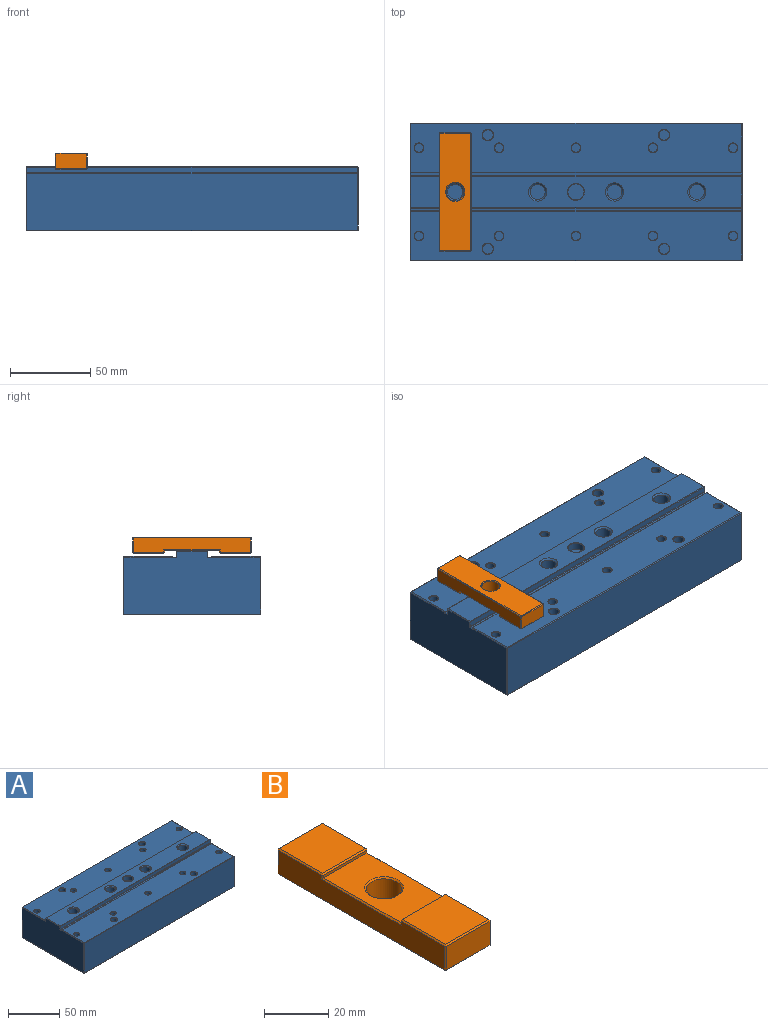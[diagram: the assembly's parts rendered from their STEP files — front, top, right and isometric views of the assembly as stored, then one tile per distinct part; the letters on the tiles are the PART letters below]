
ASSEMBLY  parts=2 mates=1
PART A: 127 faces, bbox 207.1x86x40 mm
  f0: plane 206.1x85mm, normal (0,0,-1), area 17314.4mm2, adj f68,f69,f79,f80,f110,f111
  f1: plane 206.1x30.37mm, normal (0,0,1), area 6032.9mm2, adj f10,f77,f86,f93,f120,f121,f122,f123
  f2: plane 85x39mm, normal (1,0,0), area 3080.9mm2, adj f58,f59,f60,f61,f62,f63,f65,f67
  f3: plane 85x39mm, normal (-1,0,0), area 3080.9mm2, adj f80,f81,f87,f88,f91,f93,f94,f95
  f4: plane 206.1x30.37mm, normal (0,0,1), area 6032.9mm2, adj f8,f71,f82,f88,f113,f114,f115,f116
  f5: plane 206.1x19.27mm, normal (0,0,1), area 3475mm2, adj f20,f21,f22,f23,f59,f100,f102,f103
  f6: plane 206.1x3.4mm, normal (0,-1,0), area 700.7mm2, adj f25,f61,f101,f103
  f7: plane 206.1x3.4mm, normal (0,1,0), area 700.7mm2, adj f27,f58,f98,f102
  f8: plane 206.1x0.2mm, normal (0,-1,0), area 41.2mm2, adj f4,f26,f66,f89
  f9: plane 206.1x1.6mm, normal (0,0,1), area 329.8mm2, adj f26,f27,f62,f94
  f10: plane 206.1x0.2mm, normal (0,1,0), area 41.2mm2, adj f1,f24,f72,f92
  f11: plane 206.1x1.6mm, normal (0,0,1), area 329.8mm2, adj f24,f25,f67,f97
  f12: cylinder r=4.7mm len=24mm, axis (0,0,1), area 708.7mm2, adj f13,f20
  f13: plane 9.4x9.4mm, normal (0,0,1), area 69.4mm2, adj f12
  f14: cylinder r=4.7mm len=24mm, axis (0,0,1), area 708.7mm2, adj f15,f21
  f15: plane 9.4x9.4mm, normal (0,0,1), area 69.4mm2, adj f14
  f16: cylinder r=4.7mm len=24mm, axis (0,0,1), area 708.7mm2, adj f17,f22
  f17: plane 9.4x9.4mm, normal (0,0,1), area 69.4mm2, adj f16
  f18: cylinder r=4.7mm len=24mm, axis (0,0,1), area 708.7mm2, adj f19,f23
  f19: plane 9.4x9.4mm, normal (0,0,1), area 69.4mm2, adj f18
  f20: cone r=5.7mm half-angle=45deg, axis (0,0,1), area 46.2mm2, adj f5,f12
  f21: cone r=5.7mm half-angle=45deg, axis (0,0,1), area 46.2mm2, adj f5,f14
  f22: cone r=4.7mm half-angle=45deg, axis (0,0,1), area 46.2mm2, adj f5,f16
  f23: cone r=4.7mm half-angle=45deg, axis (0,0,1), area 46.2mm2, adj f5,f18
  f24: cylinder r=0.3mm len=206.1mm, axis (1,0,0), area 97.1mm2, adj f10,f11,f73,f95
  f25: cylinder r=0.3mm len=206.1mm, axis (-1,0,0), area 97.1mm2, adj f6,f11,f63,f99
  f26: cylinder r=0.3mm len=206.1mm, axis (-1,0,0), area 97.1mm2, adj f8,f9,f65,f91
  f27: cylinder r=0.3mm len=206.1mm, axis (1,0,0), area 97.1mm2, adj f7,f9,f60,f96
  f28: cylinder r=3.25mm len=6.5mm, axis (0,0,1), area 96mm2, adj f29,f114
  f29: plane 6.5x6.5mm, normal (0,0,1), area 33.2mm2, adj f28
  f30: cylinder r=2.75mm len=5.5mm, axis (0,0,1), area 81.2mm2, adj f31,f116
  f31: plane 5.5x5.5mm, normal (0,0,1), area 23.8mm2, adj f30
  f32: cylinder r=2.75mm len=5.5mm, axis (0,0,1), area 81.2mm2, adj f33,f119
  f33: plane 5.5x5.5mm, normal (0,0,1), area 23.8mm2, adj f32
  f34: cylinder r=3.25mm len=6.5mm, axis (0,0,1), area 96mm2, adj f35,f118
  f35: plane 6.5x6.5mm, normal (0,0,1), area 33.2mm2, adj f34
  f36: cylinder r=2.75mm len=5.5mm, axis (0,0,1), area 81.2mm2, adj f37,f117
  f37: plane 5.5x5.5mm, normal (0,0,1), area 23.8mm2, adj f36
  f38: cylinder r=2.75mm len=5.5mm, axis (0,0,1), area 81.2mm2, adj f39,f113
  f39: plane 5.5x5.5mm, normal (0,0,1), area 23.8mm2, adj f38
  f40: cylinder r=2.75mm len=5.5mm, axis (0,0,1), area 81.2mm2, adj f41,f115
  f41: plane 5.5x5.5mm, normal (0,0,1), area 23.8mm2, adj f40
  f42: cylinder r=2.75mm len=5.5mm, axis (0,0,1), area 81.2mm2, adj f43,f123
  f43: plane 5.5x5.5mm, normal (0,0,1), area 23.8mm2, adj f42
  f44: cylinder r=2.75mm len=5.5mm, axis (0,0,1), area 81.2mm2, adj f45,f120
  f45: plane 5.5x5.5mm, normal (0,0,1), area 23.8mm2, adj f44
  f46: cylinder r=2.75mm len=5.5mm, axis (0,0,1), area 81.2mm2, adj f47,f124
  f47: plane 5.5x5.5mm, normal (0,0,1), area 23.8mm2, adj f46
  f48: cylinder r=3.25mm len=6.5mm, axis (0,0,1), area 96mm2, adj f49,f125
  f49: plane 6.5x6.5mm, normal (0,0,1), area 33.2mm2, adj f48
  f50: cylinder r=2.75mm len=5.5mm, axis (0,0,1), area 81.2mm2, adj f51,f122
  f51: plane 5.5x5.5mm, normal (0,0,1), area 23.8mm2, adj f50
  f52: cylinder r=3.25mm len=6.5mm, axis (0,0,1), area 96mm2, adj f53,f121
  f53: plane 6.5x6.5mm, normal (0,0,1), area 33.2mm2, adj f52
  f54: cylinder r=2.75mm len=5.5mm, axis (0,0,1), area 81.2mm2, adj f55,f126
  f55: plane 5.5x5.5mm, normal (0,0,1), area 23.8mm2, adj f54
  f56: plane 206.1x35.5mm, normal (0,-1,0), area 7316.6mm2, adj f78,f79,f86,f87
  f57: plane 206.1x35.5mm, normal (0,1,0), area 7316.6mm2, adj f69,f70,f81,f82
  f58: plane 3.55x0.5mm, normal (0.71,0.71,0), area 2.4mm2, adj f2,f7,f59,f60,f102
  f59: plane 19.57x0.5mm, normal (0.71,0,0.71), area 13.6mm2, adj f2,f5,f58,f61,f102,f103
  f60: cone r=0.8mm half-angle=45deg, axis (1,0,0), area 0.6mm2, adj f2,f27,f58,f62
  f61: plane 3.55x0.5mm, normal (0.71,-0.71,0), area 2.4mm2, adj f2,f6,f59,f63,f103
  f62: plane 1.6x0.5mm, normal (0.71,0,0.71), area 1.1mm2, adj f2,f9,f60,f65
  f63: cone r=0.8mm half-angle=45deg, axis (1,0,0), area 0.6mm2, adj f2,f25,f61,f67
  f64: plane 0.5x0.5mm, normal (0.58,0.58,-0.58), area 0.2mm2, adj f68,f69,f70
  f65: cone r=0.8mm half-angle=45deg, axis (1,0,0), area 0.6mm2, adj f2,f26,f62,f66,f71
  f66: plane 0.2x0.2mm, normal (0.71,-0.71,0), area 0mm2, adj f8,f65,f71
  f67: plane 1.6x0.5mm, normal (0.71,0,0.71), area 1.1mm2, adj f2,f11,f63,f73
  f68: plane 85x0.5mm, normal (0.71,0,-0.71), area 60.1mm2, adj f0,f2,f64,f74
  f69: plane 206.1x0.5mm, normal (0,0.71,-0.71), area 145.7mm2, adj f0,f57,f64,f75
  f70: plane 35.5x0.5mm, normal (0.71,0.71,0), area 25.1mm2, adj f2,f57,f64,f76
  f71: plane 30.41x0.55mm, normal (0.71,0,0.71), area 21.3mm2, adj f2,f4,f65,f66,f76
  f72: plane 0.2x0.2mm, normal (0.71,0.71,0), area 0mm2, adj f10,f73,f77
  f73: cone r=0.8mm half-angle=45deg, axis (1,0,0), area 0.6mm2, adj f2,f24,f67,f72,f77
  f74: plane 0.5x0.5mm, normal (0.58,-0.58,-0.58), area 0.2mm2, adj f68,f78,f79
  f75: plane 0.5x0.5mm, normal (-0.58,0.58,-0.58), area 0.2mm2, adj f69,f80,f81
  f76: plane 0.5x0.5mm, normal (0.58,0.58,0.58), area 0.2mm2, adj f70,f71,f82
  f77: plane 30.41x0.55mm, normal (0.71,0,0.71), area 21.3mm2, adj f1,f2,f72,f73,f83
  f78: plane 35.5x0.5mm, normal (0.71,-0.71,0), area 25.1mm2, adj f2,f56,f74,f83
  f79: plane 206.1x0.5mm, normal (0,-0.71,-0.71), area 145.7mm2, adj f0,f56,f74,f84
  f80: plane 85x0.5mm, normal (-0.71,0,-0.71), area 60.1mm2, adj f0,f3,f75,f84
  f81: plane 35.5x0.5mm, normal (-0.71,0.71,0), area 25.1mm2, adj f3,f57,f75,f85
  f82: plane 206.1x0.5mm, normal (0,0.71,0.71), area 145.7mm2, adj f4,f57,f76,f85
  f83: plane 0.5x0.5mm, normal (0.58,-0.58,0.58), area 0.2mm2, adj f77,f78,f86
  f84: plane 0.5x0.5mm, normal (-0.58,-0.58,-0.58), area 0.2mm2, adj f79,f80,f87
  f85: plane 0.5x0.5mm, normal (-0.58,0.58,0.58), area 0.2mm2, adj f81,f82,f88
  f86: plane 206.1x0.5mm, normal (0,-0.71,0.71), area 145.7mm2, adj f1,f56,f83,f90
  f87: plane 35.5x0.5mm, normal (-0.71,-0.71,0), area 25.1mm2, adj f3,f56,f84,f90
  f88: plane 30.41x0.55mm, normal (-0.71,0,0.71), area 21.3mm2, adj f3,f4,f85,f89,f91
  f89: plane 0.2x0.2mm, normal (-0.71,-0.71,0), area 0mm2, adj f8,f88,f91
  f90: plane 0.5x0.5mm, normal (-0.58,-0.58,0.58), area 0.2mm2, adj f86,f87,f93
  f91: cone r=0.8mm half-angle=45deg, axis (-1,0,0), area 0.6mm2, adj f3,f26,f88,f89,f94
  f92: plane 0.2x0.2mm, normal (-0.71,0.71,0), area 0mm2, adj f10,f93,f95
  f93: plane 30.41x0.55mm, normal (-0.71,0,0.71), area 21.3mm2, adj f1,f3,f90,f92,f95
  f94: plane 1.6x0.5mm, normal (-0.71,0,0.71), area 1.1mm2, adj f3,f9,f91,f96
  f95: cone r=0.8mm half-angle=45deg, axis (-1,0,0), area 0.6mm2, adj f3,f24,f92,f93,f97
  f96: cone r=0.8mm half-angle=45deg, axis (-1,0,0), area 0.6mm2, adj f3,f27,f94,f98
  f97: plane 1.6x0.5mm, normal (-0.71,0,0.71), area 1.1mm2, adj f3,f11,f95,f99
  f98: plane 3.55x0.5mm, normal (-0.71,0.71,0), area 2.4mm2, adj f3,f7,f96,f100,f102
  f99: cone r=0.8mm half-angle=45deg, axis (-1,0,0), area 0.6mm2, adj f3,f25,f97,f101
  f100: plane 19.57x0.5mm, normal (-0.71,0,0.71), area 13.6mm2, adj f3,f5,f98,f101,f102,f103
  f101: plane 3.55x0.5mm, normal (-0.71,-0.71,0), area 2.4mm2, adj f3,f6,f99,f100,f103
  f102: plane 206.4x0.3mm, normal (0,0.71,0.71), area 87.5mm2, adj f5,f7,f58,f59,f98,f100
  f103: plane 206.4x0.3mm, normal (0,-0.71,0.71), area 87.5mm2, adj f5,f6,f59,f61,f100,f101
  f104: cylinder r=5mm len=10mm, axis (0,0,1), area 147.7mm2, adj f105,f112
  f105: plane 10x10mm, normal (0,0,1), area 78.5mm2, adj f104
  f106: cylinder r=4.7mm len=19mm, axis (0,0,-1), area 561.1mm2, adj f107,f110
  f107: plane 9.4x9.4mm, normal (0,0,-1), area 69.4mm2, adj f106
  f108: cylinder r=4.7mm len=19mm, axis (0,0,-1), area 561.1mm2, adj f109,f111
  f109: plane 9.4x9.4mm, normal (0,0,-1), area 69.4mm2, adj f108
  f110: cone r=5.7mm half-angle=45deg, axis (0,0,-1), area 46.2mm2, adj f0,f106
  f111: cone r=4.7mm half-angle=45deg, axis (0,0,-1), area 46.2mm2, adj f0,f108
  f112: cone r=5mm half-angle=45deg, axis (0,0,1), area 13.7mm2, adj f5,f104
  f113: cone r=2.75mm half-angle=45deg, axis (0,0,1), area 7.7mm2, adj f4,f38
  f114: cone r=3.25mm half-angle=45deg, axis (0,0,1), area 9.1mm2, adj f4,f28
  f115: cone r=2.75mm half-angle=45deg, axis (0,0,1), area 7.7mm2, adj f4,f40
  f116: cone r=3.05mm half-angle=45deg, axis (0,0,1), area 7.7mm2, adj f4,f30
  f117: cone r=3.05mm half-angle=45deg, axis (0,0,1), area 7.7mm2, adj f4,f36
  f118: cone r=3.55mm half-angle=45deg, axis (0,0,1), area 9.1mm2, adj f4,f34
  f119: cone r=3.05mm half-angle=45deg, axis (0,0,1), area 7.7mm2, adj f4,f32
  f120: cone r=2.75mm half-angle=45deg, axis (0,0,1), area 7.7mm2, adj f1,f44
  f121: cone r=3.25mm half-angle=45deg, axis (0,0,1), area 9.1mm2, adj f1,f52
  f122: cone r=2.75mm half-angle=45deg, axis (0,0,1), area 7.7mm2, adj f1,f50
  f123: cone r=3.05mm half-angle=45deg, axis (0,0,1), area 7.7mm2, adj f1,f42
  f124: cone r=3.05mm half-angle=45deg, axis (0,0,1), area 7.7mm2, adj f1,f46
  f125: cone r=3.55mm half-angle=45deg, axis (0,0,1), area 9.1mm2, adj f1,f48
  f126: cone r=3.05mm half-angle=45deg, axis (0,0,1), area 7.7mm2, adj f1,f54
PART B: 47 faces, bbox 20x74x10 mm
  f0: plane 19x19mm, normal (0,0,1), area 361mm2, adj f33,f34,f40,f41
  f1: plane 19x19mm, normal (0,0,1), area 361mm2, adj f18,f19,f30,f31
  f2: plane 73x9mm, normal (-1,0,0), area 604.5mm2, adj f12,f14,f18,f23,f24,f29,f34,f35
  f3: plane 19x9mm, normal (0,1,0), area 171mm2, adj f12,f13,f19,f20
  f4: plane 19x9mm, normal (0,-1,0), area 171mm2, adj f22,f23,f32,f33
  f5: plane 73x9mm, normal (1,0,0), area 604.5mm2, adj f20,f21,f31,f32,f39,f40,f42,f44
  f6: plane 73x19mm, normal (0,0,-1), area 1273.9mm2, adj f13,f14,f21,f22,f45
  f7: plane 19x1mm, normal (0,1,0), area 19mm2, adj f9,f35,f41,f44
  f8: plane 19x1mm, normal (0,-1,0), area 19mm2, adj f9,f24,f30,f39
  f9: plane 34x19mm, normal (0,0,1), area 532.9mm2, adj f7,f8,f29,f42,f46
  f10: cylinder r=5.5mm len=11mm, axis (0,0,1), area 259.2mm2, adj f45,f46
  f11: plane 0.5x0.5mm, normal (-0.58,0.58,-0.58), area 0.2mm2, adj f12,f13,f14
  f12: plane 9x0.5mm, normal (-0.71,0.71,0), area 6.4mm2, adj f2,f3,f11,f15
  f13: plane 19x0.5mm, normal (0,0.71,-0.71), area 13.4mm2, adj f3,f6,f11,f16
  f14: plane 73x0.5mm, normal (-0.71,0,-0.71), area 51.6mm2, adj f2,f6,f11,f17
  f15: plane 0.5x0.5mm, normal (-0.58,0.58,0.58), area 0.2mm2, adj f12,f18,f19
  f16: plane 0.5x0.5mm, normal (0.58,0.58,-0.58), area 0.2mm2, adj f13,f20,f21
  f17: plane 0.5x0.5mm, normal (-0.58,-0.58,-0.58), area 0.2mm2, adj f14,f22,f23
  f18: plane 19x0.5mm, normal (-0.71,0,0.71), area 13.4mm2, adj f1,f2,f15,f25
  f19: plane 19x0.5mm, normal (0,0.71,0.71), area 13.4mm2, adj f1,f3,f15,f26
  f20: plane 9x0.5mm, normal (0.71,0.71,0), area 6.4mm2, adj f3,f5,f16,f26
  f21: plane 73x0.5mm, normal (0.71,0,-0.71), area 51.6mm2, adj f5,f6,f16,f27
  f22: plane 19x0.5mm, normal (0,-0.71,-0.71), area 13.4mm2, adj f4,f6,f17,f27
  f23: plane 9x0.5mm, normal (-0.71,-0.71,0), area 6.4mm2, adj f2,f4,f17,f28
  f24: plane 1.5x0.5mm, normal (-0.71,-0.71,0), area 0.9mm2, adj f2,f8,f25,f29
  f25: plane 0.5x0.5mm, normal (-0.58,-0.58,0.58), area 0.2mm2, adj f18,f24,f30
  f26: plane 0.5x0.5mm, normal (0.58,0.58,0.58), area 0.2mm2, adj f19,f20,f31
  f27: plane 0.5x0.5mm, normal (0.58,-0.58,-0.58), area 0.2mm2, adj f21,f22,f32
  f28: plane 0.5x0.5mm, normal (-0.58,-0.58,0.58), area 0.2mm2, adj f23,f33,f34
  f29: plane 35x0.5mm, normal (-0.71,0,0.71), area 24.4mm2, adj f2,f9,f24,f35
  f30: plane 19x0.5mm, normal (0,-0.71,0.71), area 13.4mm2, adj f1,f8,f25,f36
  f31: plane 19x0.5mm, normal (0.71,0,0.71), area 13.4mm2, adj f1,f5,f26,f36
  f32: plane 9x0.5mm, normal (0.71,-0.71,0), area 6.4mm2, adj f4,f5,f27,f37
  f33: plane 19x0.5mm, normal (0,-0.71,0.71), area 13.4mm2, adj f0,f4,f28,f37
  f34: plane 19x0.5mm, normal (-0.71,0,0.71), area 13.4mm2, adj f0,f2,f28,f38
  f35: plane 1.5x0.5mm, normal (-0.71,0.71,0), area 0.9mm2, adj f2,f7,f29,f38
  f36: plane 0.5x0.5mm, normal (0.58,-0.58,0.58), area 0.2mm2, adj f30,f31,f39
  f37: plane 0.5x0.5mm, normal (0.58,-0.58,0.58), area 0.2mm2, adj f32,f33,f40
  f38: plane 0.5x0.5mm, normal (-0.58,0.58,0.58), area 0.2mm2, adj f34,f35,f41
  f39: plane 1.5x0.5mm, normal (0.71,-0.71,0), area 0.9mm2, adj f5,f8,f36,f42
  f40: plane 19x0.5mm, normal (0.71,0,0.71), area 13.4mm2, adj f0,f5,f37,f43
  f41: plane 19x0.5mm, normal (0,0.71,0.71), area 13.4mm2, adj f0,f7,f38,f43
  f42: plane 35x0.5mm, normal (0.71,0,0.71), area 24.4mm2, adj f5,f9,f39,f44
  f43: plane 0.5x0.5mm, normal (0.58,0.58,0.58), area 0.2mm2, adj f40,f41,f44
  f44: plane 1.5x0.5mm, normal (0.71,0.71,0), area 0.9mm2, adj f5,f7,f42,f43
  f45: cone r=6mm half-angle=45deg, axis (0,0,-1), area 25.5mm2, adj f6,f10
  f46: cone r=5.5mm half-angle=45deg, axis (0,0,1), area 25.5mm2, adj f9,f10
PLACE A t=(-47.99,-20.56,-9.28)mm
PLACE B rot(axis=(1,0,0),180deg) t=(-123.36,-20.56,39.22)mm
MATE fastened B.f10 <-> A.f18  axis (0,0,-1) through (-123.36,-20.56,31.22)mm
